# Revit family: INGROUND 12W RGBW_LKPA2BE0320.22
name_source: partatom
category: Luminarias
units: mm (PartAtom-declared; Revit-internal decimal feet)

## family parameters
Compartido = No
Corte con vacíos al cargar = No
Cota de conector redondo = Diámetro de uso
Origen de luz = Sí
Punto de cálculo de habitación = No
Se basa en plano de trabajo = Sí
Siempre vertical = No
Tipo de pieza = Normal

## types (1)
- EMP_LKPA2BE0320.22
    Cambio de temperatura de color de luz atenuada = <Ninguno>
    Comentarios de vataje = 24V
    Descripción = LUMINARIA TIPO CIRCULAR PARA EMPOTRAR EN PISO CON CUERPO DE ALUMINIO FUNDIDO A PRESION CUBIERTO CON POLVO GRIS OSCURO, CON CUBIERTA DE ACERO INOXIDABLE Y VIDRIO TEMPLADO DE 8MM, HOUSING PVC DE 156.5MM DE DIAMETRO Y 149.5MM DE PROFUNDO. CUENTA CON 3 LED CON UNA POTENCIA TOTAL DE 14.6W, TECNOLOGIA RGBW CON 430 LUMENES, 610mA EN CORRIENTE DE OPERACIÓN, IP67, IK07, APERTURA EN 22 GRADOS POR STOCK, ALIMENTADA A 24V. REQUIERE ACCESORIOS.
    Elevación por defecto = 0 mm  [stored 0 ft]
    Fabricante = BRILLANT
    Filtro de color = 16777215
    Longitud de símbolo de origen de luz = 500 mm  [stored 1.64042 ft]
    Lámpara = RGBW
    Modelo = LKPA2BE0320.22
    Watt per fixture = 14.6
    Ángulo de campo de foco = 22.00°
    Ángulo de enfoque = 22.00°
    Ángulo de inclinación = 105.00°

note: [stored X ft] marks values corroborated as IEEE doubles in the binary element streams (Revit-internal decimal feet)

## geometry (parser evidence)
native form markers: Blend x2
no freeform markers — native parametric forms only
